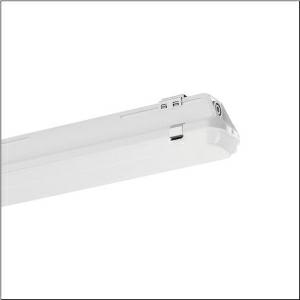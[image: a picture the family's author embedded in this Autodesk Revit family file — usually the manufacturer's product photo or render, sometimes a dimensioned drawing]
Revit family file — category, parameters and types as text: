
# Revit family: monsun_r__11_facade_51ff40dp460l007_266d
name_source: partatom
category: Lighting Fixtures
units: mm (PartAtom-declared; Revit-internal decimal feet)

## family parameters
Cut with Voids When Loaded = No
Host = Face
Light Source = No
Part Type = Normal
Room Calculation Point = No
Round Connector Dimension = Use Diameter
Shared = No

## types (1)
- --- (1 x LED, 6190 lm, 31.8 W, 4000K)
    Apparent Load = 32 VA
    CIE Flux Codes = 47 77 93 95 100
    Color Rendering = 80
    Color Temperature = 4000K
    Default Elevation = 1800 mm
    Description = Monsun® 11 facade, damp-proof luminaire, chain hanger, primary optical cover: enclosure, of PMMA, light emission: direct distribution, primary light characteristic: symmetric, installation type: surface-mounted, horizontal mounting, vertical mounting, LED, rated luminous flux: 6.190lm, luminous efficacy: 195lm/W, light colour: 840, colour temperature: 4000K, control gear: DALI 2, with terminal, 5-pole, max. 2.5mm², through-wiring: 7x 2.5mm², mains connection: 220..240V, AC, 50/60Hz, rated input power: 32W, housing, of glass-fibre reinforced polyester, uncoated, bright grey, incl. chain hanger, for cables, Ø 8.4..12mm, with climate membrane, length: 1.590mm, width: 90mm, height: 88mm, clip for enclosure, of stainless steel (V2A), ceiling mounting element, of stainless steel (V2A), chain hanger, of stainless steel (V2A), protection rating (complete): IP66, insulation class (complete): insulation class I (protective earthing), certification: CE, ENEC, VDE, UKCA, protection symbol: D, impact resistance: IK06, permissible operating ambient temperature: -35..+50°C, standard: EN 50419, EN 60598-2-1, contact your sales advisor before using the luminaires in applications with unclear chemical exposure, large temperature fluctuations or condensation-forming humidity, LABS conformity tested according to VDMA 24364:2018-05, exposed outdoor area, packaging unit: 1 piece
    Height = 89 mm
    Lamp = 1 x LED
    Lamp Light Flux = 6190 lm
    Lamp Power = 31.8 W
    Lamp count = 1
    Length = 1590 mm
    Luminous efficacy = 195 lm/W
    Manufacturer = Siteco
    ModVariant = No
    Model = 51FF40DP460L007
    Mounting Place = Ceiling
    Mounting Type = Surface mounted
    Number of Poles = 1
    OnlyDefault = Yes
    Power Factor = 1
    Product Name = Monsun® 11 facade
    Product group = damp-proof luminaire
    ProductGroupID = 300
    Protection Class = Protection class I
    Protection Degree = IP 66
    RLX_Detail_Level = 1
    RLX_Emergency_Light_Flux = 0 lm
    RLX_Emergency_Type = 0
    RLX_Emergency_Type_DB = No
    RlxData = <blob elided: 92373 chars, md5=c0b9ba1f>
    Socket = socket
    Standby Power = 0 W
    System Light Flux = 6190 lm
    System Power = 32 W
    Type Comments = factory setting: luminous flux: 100 % | dim-lin: 254 | 221 mA
    Type Image = l_1349237.jpg
    URL = http://relux.com
    VarID = @adj_018362
    Voltage = 0 V
    Weight = 0.00 kg
    Width = 90 mm

## geometry (parser evidence)
native form markers: Blend x4, Sweep x14
no freeform markers — native parametric forms only
